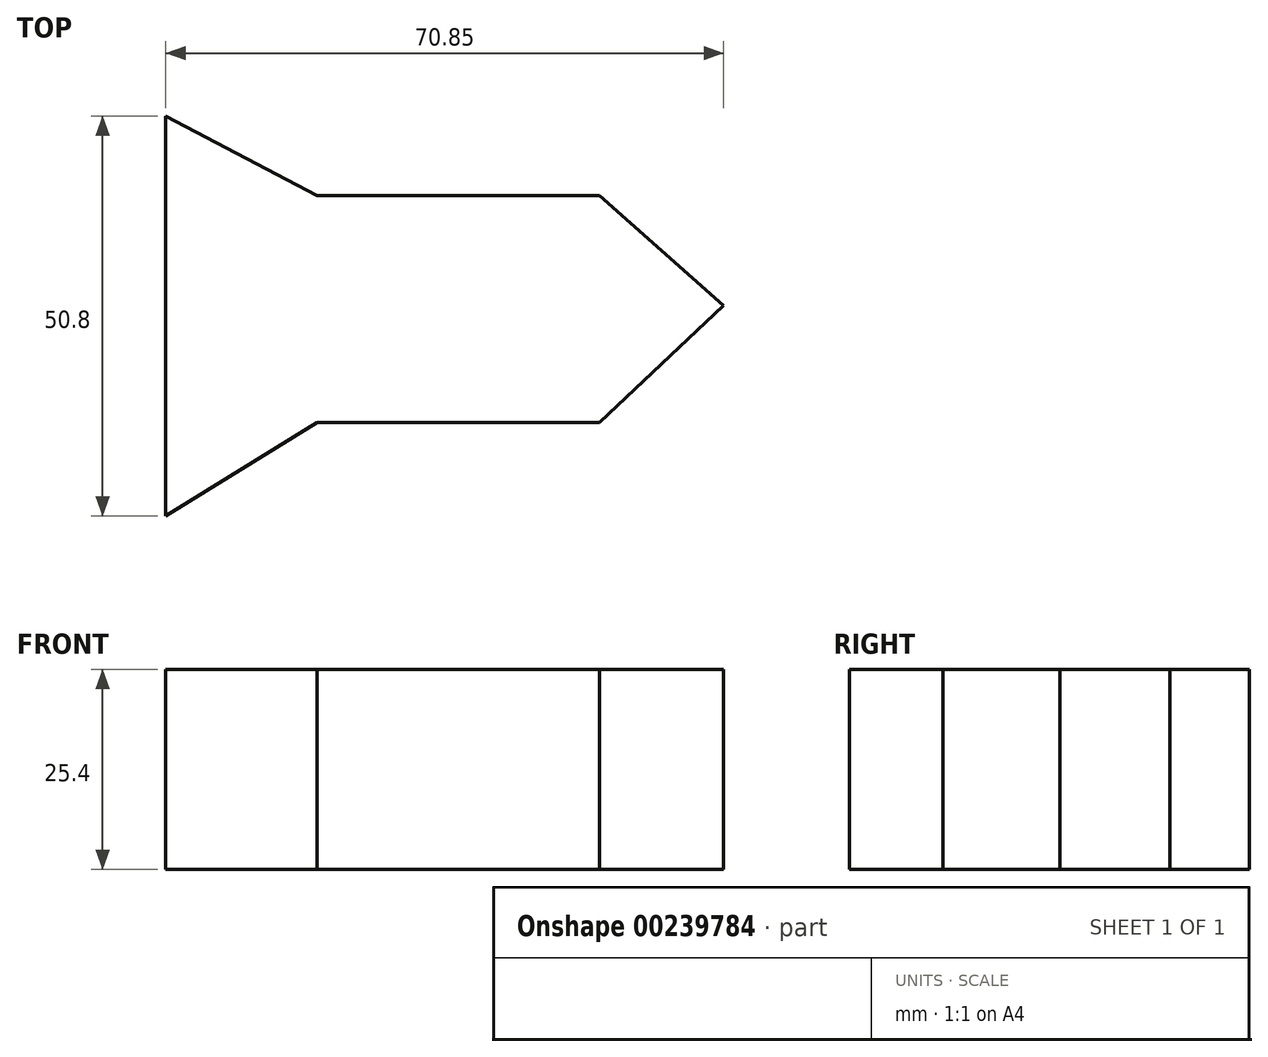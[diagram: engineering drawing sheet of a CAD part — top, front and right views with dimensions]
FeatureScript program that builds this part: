
annotation { "Feature Type Name" : "Feature", "Feature Type Description" : "" }
export const myFeature = defineFeature(function(context is Context, id is Id, definition is map)
    precondition{}
    {
        {
            var Q0;
            Q0=qCreatedBy(makeId("Top.planeOp"),FACE);
            var sketch = newSketch(context, id + "F0", { "sketchPlane" : qUnion([Q0])});
            skLineSegment(sketch, "E0", {"start": v(0, 24.04) * mm, "end": v(0, -26.76) * mm});
            skPoint(sketch, "E1", {"position": v(0, -14.52) * mm});
            skPoint(sketch, "E2", {"position": v(0, 12.12) * mm});
            skLineSegment(sketch, "E3", {"start": v(0, -26.76) * mm, "end": v(19.24, -14.9) * mm});
            skLineSegment(sketch, "E4", {"start": v(19.24, -14.9) * mm, "end": v(55.13, -14.9) * mm});
            skLineSegment(sketch, "E5", {"start": v(55.13, -14.9) * mm, "end": v(70.85, 0) * mm});
            skLineSegment(sketch, "E6", {"start": v(70.85, 0) * mm, "end": v(55.13, 13.97) * mm});
            skLineSegment(sketch, "E7", {"start": v(19.24, 13.97) * mm, "end": v(55.13, 13.97) * mm});
            skLineSegment(sketch, "E8", {"start": v(19.24, 13.97) * mm, "end": v(0, 24.04) * mm});
            skSolve(sketch);
        }
        {
            var Q0;
            Q0 = qSketchRegion(id + "F0", true);
            extrude(context, id + "F1", {"entities" : qUnion([Q0]), "depth" : 25.4 * mm});
        }
    });
